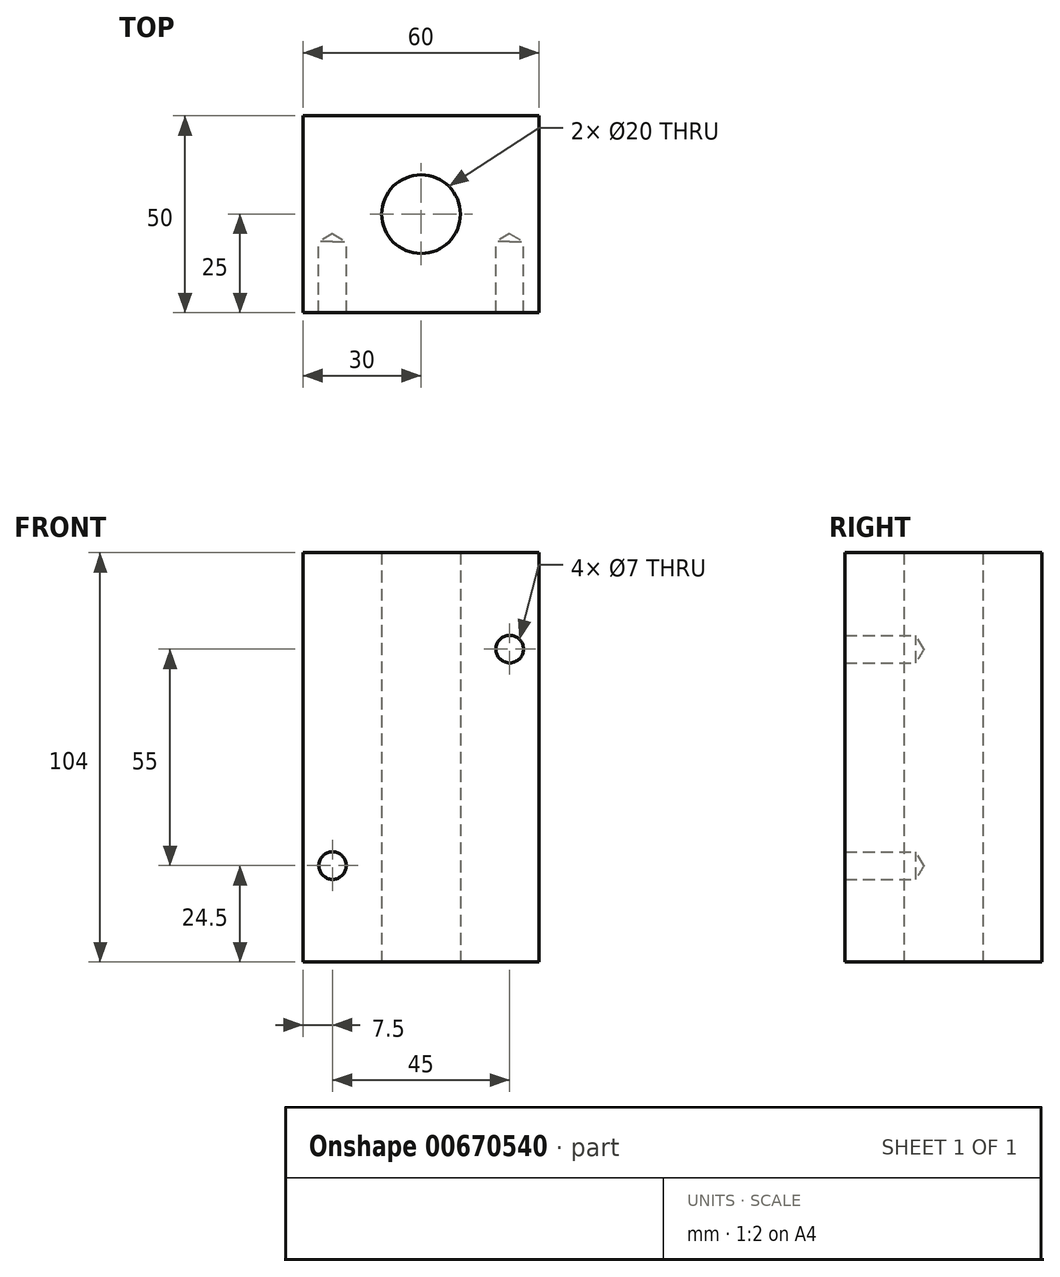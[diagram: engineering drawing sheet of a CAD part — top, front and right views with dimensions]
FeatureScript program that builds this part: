
annotation { "Feature Type Name" : "Feature", "Feature Type Description" : "" }
export const myFeature = defineFeature(function(context is Context, id is Id, definition is map)
    precondition{}
    {
        {
            var Q0;
            Q0=qCreatedBy(makeId("Top.planeOp"),FACE);
            var sketch = newSketch(context, id + "F0", { "sketchPlane" : qUnion([Q0])});
            skLineSegment(sketch, "E0.bottom", {"start": v(-30, 25) * mm, "end": v(30, 25) * mm});
            skLineSegment(sketch, "E0.top", {"start": v(-30, -25) * mm, "end": v(30, -25) * mm});
            skLineSegment(sketch, "E0.left", {"start": v(-30, 25) * mm, "end": v(-30, -25) * mm});
            skLineSegment(sketch, "E0.right", {"start": v(30, 25) * mm, "end": v(30, -25) * mm});
            skCircle(sketch, "E1", {"center": v(0, 0) * mm, "radius": 10 * mm});
            skSolve(sketch);
        }
        {
            var Q0;
            Q0=makeQuery(id+"F0.imprint","IMPRINT",FACE,{"disambiguationData":[TD([[makeQuery(id+"F0.imprint","IMPRINT",EDGE,{"derivedFrom":sQuery(id+"F0.wireOp",EDGE,"E0.bottom")}),-1.0]])]});
            extrude(context, id + "F1", {"entities" : qUnion([Q0]), "depth" : 104 * mm, "offsetDistance" : 25 * mm, "symmetric" : true});
        }
        {
            var Q0;
            Q0=makeQuery(id+"F1.opExtrude","SWEPT_FACE",FACE,{"disambiguationData":[OSD([sQuery(id+"F0.wireOp",EDGE,"E0.top")])]});
            var sketch = newSketch(context, id + "F2", { "sketchPlane" : qUnion([Q0])});
            skPoint(sketch, "E2", {"position": v(22.5, 27.5) * mm});
            skPoint(sketch, "E3", {"position": v(-22.5, -27.5) * mm});
            skSolve(sketch);
        }
        {
            var Q0;
            Q0=sQuery(id+"F2.wireOp",VERTEX,"E2");
            var Q1;
            Q1=sQuery(id+"F2.wireOp",VERTEX,"E3");
            var Q2;
            Q2=makeQuery(id+"F1.opExtrude","SWEPT_BODY",BODY,{"disambiguationData":[OSD([sQuery(id+"F0.wireOp",EDGE,"E0.bottom"),sQuery(id+"F0.wireOp",EDGE,"E0.top"),sQuery(id+"F0.wireOp",EDGE,"E0.left"),sQuery(id+"F0.wireOp",EDGE,"E0.right"),sQuery(id+"F0.wireOp",EDGE,"E1")])]});
            hole(context, id + "F3", {"style" : HoleStyle.SIMPLE, "endStyle" : HoleEndStyle.BLIND, "standardTappedOrClearance" : lookupTablePath({ "standard" : "ISO", "engagement" : "75%", "pitch" : "1 mm", "size" : "M8", "type" : "Tapped" }), "standardBlindInLast" : lookupTablePath({ "standard" : "ISO", "engagement" : "75%", "pitch" : "1 mm", "size" : "M8", "type" : "Tapped" }), "holeDiameter" : 7 * mm, "majorDiameter" : 8 * mm, "showTappedDepth" : true, "holeDepth" : 18 * mm, "isTappedThrough" : true, "tappedDepth" : 15 * mm, "tapClearance" : 3, "locations" : qUnion([Q0, Q1]), "scope" : qUnion([Q2]), "startStyle" : HoleStartStyle.PART});
        }
    });
